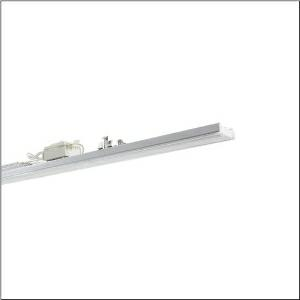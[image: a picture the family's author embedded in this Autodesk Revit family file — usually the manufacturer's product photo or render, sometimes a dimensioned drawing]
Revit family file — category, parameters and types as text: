
# Revit family: licross_r__21_recessed_ho_52te18cn4c5m_57f1
name_source: partatom
category: Lighting Fixtures
units: mm (PartAtom-declared; Revit-internal decimal feet)

## family parameters
Cut with Voids When Loaded = No
Host = Face
Light Source = No
Part Type = Normal
Room Calculation Point = No
Round Connector Dimension = Use Diameter
Shared = No

## types (1)
- --- (1 x LED, 12540 lm, 68.4 W, 4000K)
    Apparent Load = 68 VA
    CIE Flux Codes = 75 94 99 100 100
    Color Rendering = 80
    Color Temperature = 4000K
    Default Elevation = 1800 mm
    Description = Licross® 21 Recessed HO, luminaire insert, of sheet steel, galvanised, coil coated, white, length: 1.500mm, width: 66mm, height: 67mm, LED rated luminous flux: 12.540lm, light colour: 840, control gear: ON/OFF Multilumen, CLOi, control gear: ECG Multilumen, with plug, 3-pole, with phase selection, mains connection: 220..240V, AC, 50/60Hz, start of lifetime: 68W, end of service life: 83W, halogen-free wiring, primary light control with lens, of plastic, primary optical cover: cover, of PMMA, light emission: direct distribution, primary light characteristic: symmetric, protection rating (complete): IP54, insulation class (complete): insulation class I (protective earthing), certification: CE, ENEC, VDE, UKCA, protection symbol: D if used in an environment with non-conductive dust loads with corresponding accessories, impact resistance: IK06, permissible ambient temperature for indoor applications: -35..+30°C, corresponds to IFS (International Featured Standards) requirements for safety and quality in the food industry, reducing of maximum allowable ambient temperature of 5°C with ceiling mounting, LABS conformity tested according to VDMA 24364:2018-05, packaging unit: 1 piece
    Height = 58 mm
    Lamp = 1 x LED
    Lamp Light Flux = 12540 lm
    Lamp Power = 68.4 W
    Lamp count = 1
    Length = 1500 mm
    Luminous efficacy = 183 lm/W
    Manufacturer = Siteco
    ModVariant = No
    Model = 52TE18CN4C5M
    Mounting Place = Ceiling
    Mounting Type = Pendant
    Number of Poles = 1
    OnlyDefault = Yes
    Power Factor = 1
    Product Name = Licross® 21 Recessed HO
    Product group = luminaire insert
    ProductGroupID = 902
    Protection Class = Protection class I
    Protection Degree = IP 54
    RLX_Detail_Level = 1
    RLX_Emergency_Light_Flux = 0 lm
    RLX_Emergency_Type = 0
    RLX_Emergency_Type_DB = No
    RlxData = <blob elided: 22361 chars, md5=a8ac03b9>
    Socket = socket
    Standby Power = 0 W
    System Light Flux = 12540 lm
    System Power = 68 W
    Type Comments = factory setting: luminous flux: 100 % | (A | C | E) | 161 mA
    Type Image = l_1296930.jpg
    URL = http://relux.com
    VarID = @adj_109986
    Voltage = 0 V
    Weight = 0.00 kg
    Width = 66 mm

## geometry (parser evidence)
native form markers: Blend x4, Sweep x10
no freeform markers — native parametric forms only
